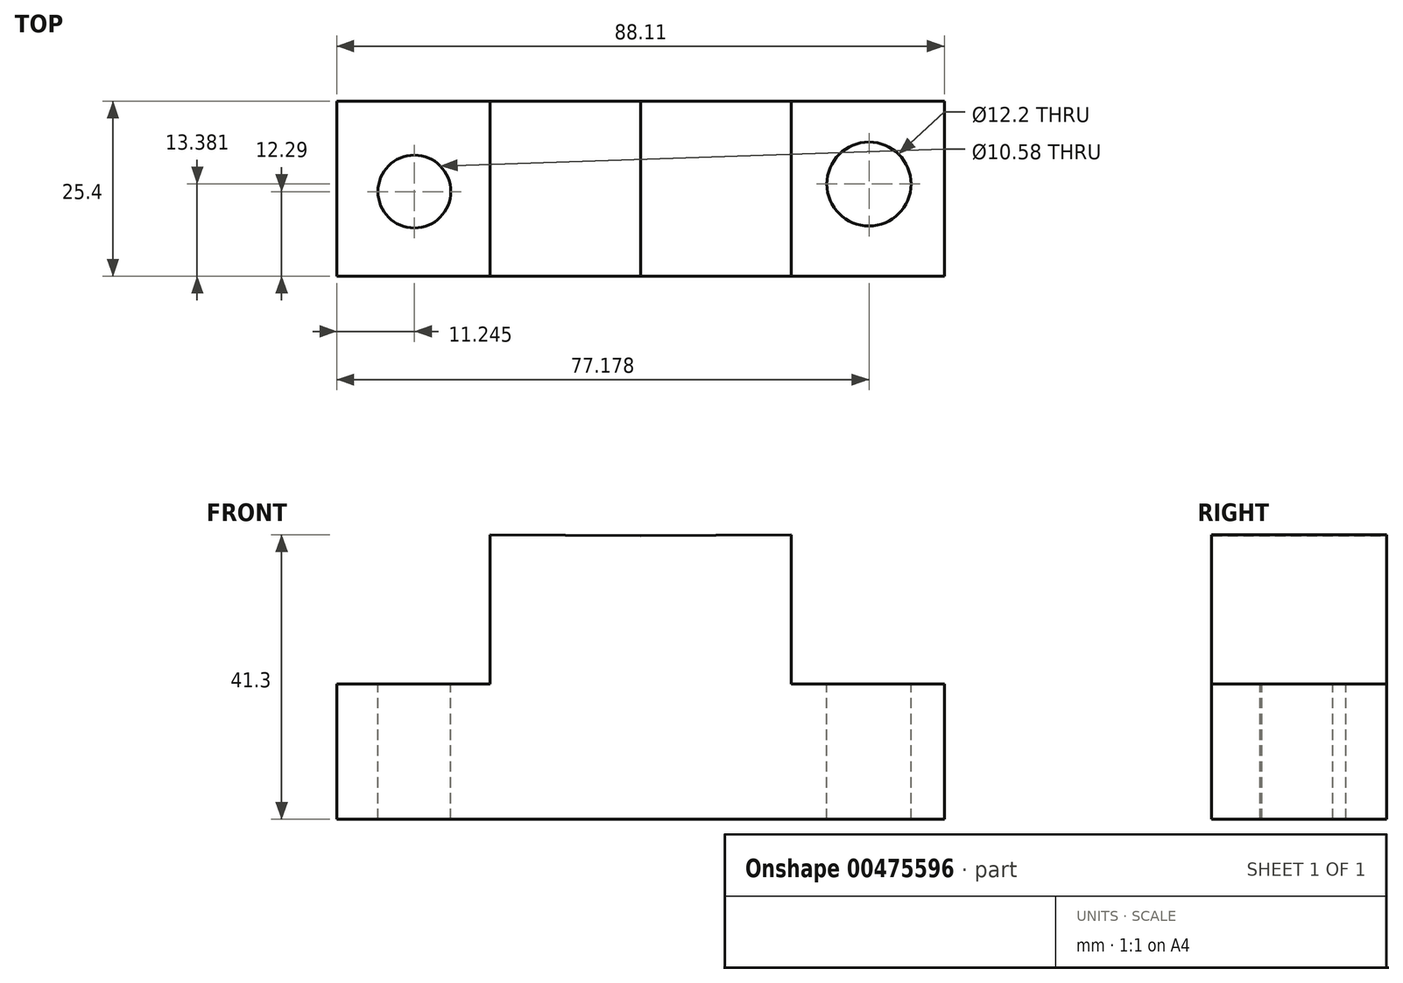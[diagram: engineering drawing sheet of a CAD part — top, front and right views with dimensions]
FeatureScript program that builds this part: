
annotation { "Feature Type Name" : "Feature", "Feature Type Description" : "" }
export const myFeature = defineFeature(function(context is Context, id is Id, definition is map)
    precondition{}
    {
        {
            var Q0;
            Q0=qCreatedBy(makeId("Front.planeOp"),FACE);
            var sketch = newSketch(context, id + "F0", { "sketchPlane" : qUnion([Q0])});
            skLineSegment(sketch, "E0", {"start": v(0, 0) * mm, "end": v(0, 21.7) * mm});
            skLineSegment(sketch, "E1", {"start": v(10.69, -19.6) * mm, "end": v(-22.19, -19.6) * mm});
            skLineSegment(sketch, "E2", {"start": v(-22.19, -19.6) * mm, "end": v(-22.19, 0) * mm});
            skLineSegment(sketch, "E3", {"start": v(-22.19, 0) * mm, "end": v(0, 0) * mm});
            skLineSegment(sketch, "E4", {"start": v(10.69, -19.6) * mm, "end": v(21.87, -19.6) * mm});
            skLineSegment(sketch, "E5", {"start": v(21.87, -19.6) * mm, "end": v(21.87, 21.54) * mm});
            skLineSegment(sketch, "E6", {"start": v(21.87, 21.54) * mm, "end": v(0, 21.7) * mm});
            skLineSegment(sketch, "E7.MirrorCS", {"start": v(21.87, 21.54) * mm, "end": v(43.73, 21.7) * mm});
            skLineSegment(sketch, "E8.MirrorCS", {"start": v(43.73, 0) * mm, "end": v(43.73, 21.7) * mm});
            skLineSegment(sketch, "E9.MirrorCS", {"start": v(65.92, 0) * mm, "end": v(43.73, 0) * mm});
            skLineSegment(sketch, "E10.MirrorCS", {"start": v(65.92, -19.6) * mm, "end": v(65.92, 0) * mm});
            skLineSegment(sketch, "E11.MirrorCS", {"start": v(33.04, -19.6) * mm, "end": v(65.92, -19.6) * mm});
            skLineSegment(sketch, "E12.MirrorCS", {"start": v(33.04, -19.6) * mm, "end": v(21.87, -19.6) * mm});
            skSolve(sketch);
        }
        {
            var Q0;
            Q0=makeQuery(id+"F0.imprint","IMPRINT",FACE,{"disambiguationData":[TD([[makeQuery(id+"F0.imprint","IMPRINT",EDGE,{"derivedFrom":sQuery(id+"F0.wireOp",EDGE,"E0")}),-1.0]])]});
            extrude(context, id + "F1", {"entities" : qUnion([Q0]), "depth" : 25.4 * mm});
        }
        {
            var Q0;
            Q0=qCreatedBy(makeId("Top.planeOp"),FACE);
            var sketch = newSketch(context, id + "F2", { "sketchPlane" : qUnion([Q0])});
            skCircle(sketch, "E13", {"center": v(-10.95, -13.11) * mm, "radius": 5.29 * mm});
            skSolve(sketch);
        }
        {
            var Q0;
            Q0 = qSketchRegion(id + "F0", true);
            extrude(context, id + "F3", {"entities" : qUnion([Q0]), "operationType" : NewBodyOperationType.ADD, "depth" : 25.4 * mm});
        }
        {
            var Q0;
            Q0=qCreatedBy(makeId("Top.planeOp"),FACE);
            var sketch = newSketch(context, id + "F4", { "sketchPlane" : qUnion([Q0])});
            skCircle(sketch, "E14", {"center": v(54.99, -12.02) * mm, "radius": 6.1 * mm});
            skSolve(sketch);
        }
        {
            var Q0;
            Q0=qCreatedBy(makeId("Top.planeOp"),FACE);
            var sketch = newSketch(context, id + "F5", { "sketchPlane" : qUnion([Q0])});
            skSolve(sketch);
        }
        {
            var Q0;
            Q0 = qSketchRegion(id + "F5", true);
            var Q1;
            Q1=makeQuery(id+"F4.imprint","IMPRINT",FACE,{"disambiguationData":[TD([[makeQuery(id+"F4.imprint","IMPRINT",EDGE,{"derivedFrom":sQuery(id+"F4.wireOp",EDGE,"E14")}),1.0]])]});
            extrude(context, id + "F6", {"entities" : qUnion([Q0, Q1]), "operationType" : NewBodyOperationType.REMOVE, "oppositeDirection" : true, "depth" : 50.8 * mm});
        }
        {
            var Q0;
            Q0=qCreatedBy(makeId("Front.planeOp"),FACE);
            var sketch = newSketch(context, id + "F7", { "sketchPlane" : qUnion([Q0])});
            skSolve(sketch);
        }
        {
            var Q0;
            Q0 = qSketchRegion(id + "F7", true);
            var Q1;
            Q1=makeQuery(id+"F2.imprint","IMPRINT",FACE,{"disambiguationData":[TD([[makeQuery(id+"F2.imprint","IMPRINT",EDGE,{"derivedFrom":sQuery(id+"F2.wireOp",EDGE,"E13")}),1.0]])]});
            extrude(context, id + "F8", {"entities" : qUnion([Q0, Q1]), "operationType" : NewBodyOperationType.REMOVE, "oppositeDirection" : true, "depth" : 25.4 * mm});
        }
    });
